# Revit family: IS_Eurovit_K2844_BIM_BE
name_source: partatom
category: Plumbing Fixtures
revit_build: Autodesk Revit 2015 (Build: 20140606_1530(x64)
units: mm (PartAtom-declared; Revit-internal decimal feet)

## types (1)
- K284401 - Astor WC suspendu rimless
    Accesoires = www.idealstandard.be
    Afwerking = Wit
    Auteur = Ideal Standard Produktions-GmbH
    Barcode = 4015413065108
    Beschrijvinggarantie = Fabrieksgarantie
    BimObjectNaam = ISI_IdealStandard_WC_Astor_K284401
    Breedte = 0
    BrutoGewicht = 0
    Cost = 0 $
    Default Elevation = 400 mm
    Description = Astor WC suspendu rimless
    Diepte = 0 mm  [stored 0 ft]
    Dimensions = 520 x 355 x 370 mm
    DuurEenheid = jaar
    Eigenschappen = Astor/ Eurovit+ wand-WC zonder spoelrand. DIN EN997. Volledig geglazuurd. Geschikt voor een spoeling vanaf 4.5L
    Garantieonderdelen = 10
    Hauteur = 370 mm
    IfcExportAs = IfcSanitaryTerminalType
    IfcExportType = TOILETPANS
    Installatieinstructies = www.idealstandard.be
    Kleur = Wit
    Kleurwc = Wit
    Largeur = 355 mm
    Lengte = 0 mm  [stored 0 ft]
    Longueur = 520 mm  [stored 1.70604 ft]
    Manufacturer = www.idealstandard.be
    Materiaal = porselein
    MateriaalWC = porselein
    Merk = Ideal Standard
    Model = K284401
    Nettogewicht = 16
    Normen = DIN EN997
    Overloop = 0 mm  [stored 0 ft]
    Productinformatie = www.idealstandard.be
    Telefoonnummer = 0032 2 325 66 00
    Testdruk = 0
    TypeWC = Wand-WC
    Typeconnectie = Sanitair
    TypespoelingWC = Diepspoel
    URL = www.idealstandard.be
    Uniclass2015Beschrijving = WC pans
    Uniclass2015Referentie = Pr_40_20_93_94
    Uniclass2015Version = Products v1.1
    Urlproducent = www.idealstandard.be
    Versie = 1
    Vervangingskosten = 0
    Verwachtelevensduur = 25 jaar
    Volumeunits = liter

note: [stored X ft] marks values corroborated as IEEE doubles in the binary element streams (Revit-internal decimal feet)

## geometry (parser evidence)
native form markers: Blend x4, Sweep x1
no freeform markers — native parametric forms only
